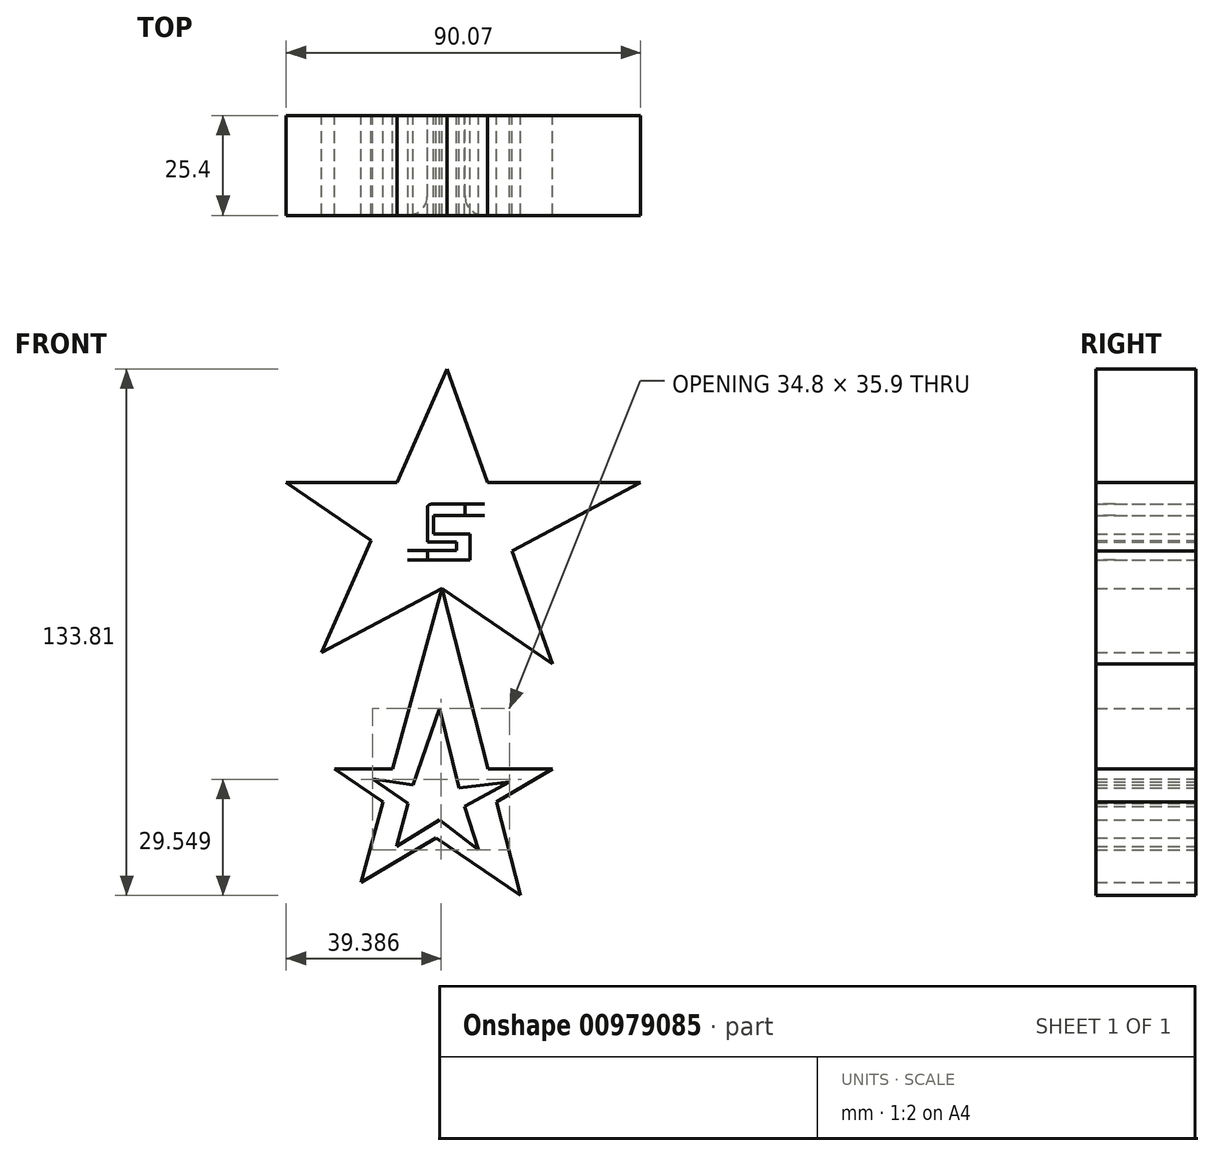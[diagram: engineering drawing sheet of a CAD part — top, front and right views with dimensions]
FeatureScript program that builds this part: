
annotation { "Feature Type Name" : "Feature", "Feature Type Description" : "" }
export const myFeature = defineFeature(function(context is Context, id is Id, definition is map)
    precondition{}
    {
        {
            var Q0;
            Q0=qCreatedBy(makeId("Front.planeOp"),FACE);
            var sketch = newSketch(context, id + "F0", { "sketchPlane" : qUnion([Q0])});
            skLineSegment(sketch, "E0", {"start": v(46.3, 35.13) * mm, "end": v(-40.9, 35.13) * mm});
            skLineSegment(sketch, "E1", {"start": v(-40.9, 35.13) * mm, "end": v(26.84, -10.99) * mm});
            skLineSegment(sketch, "E2", {"start": v(26.84, -10.99) * mm, "end": v(0, 63.95) * mm});
            skLineSegment(sketch, "E3", {"start": v(0, 63.95) * mm, "end": v(-31.89, -8.1) * mm});
            skLineSegment(sketch, "E4", {"start": v(-31.89, -8.1) * mm, "end": v(49.18, 35.13) * mm});
            skLineSegment(sketch, "E5", {"start": v(26.84, -37.65) * mm, "end": v(-28.64, -37.65) * mm});
            skLineSegment(sketch, "E6", {"start": v(-28.64, -37.65) * mm, "end": v(18.67, -69.86) * mm});
            skLineSegment(sketch, "E7", {"start": v(18.67, -69.86) * mm, "end": v(-1.33, 8.2) * mm});
            skLineSegment(sketch, "E8", {"start": v(-1.33, 8.2) * mm, "end": v(-21.8, -66.47) * mm});
            skLineSegment(sketch, "E9", {"start": v(-21.8, -66.47) * mm, "end": v(26.84, -37.65) * mm});
            skLineSegment(sketch, "E10", {"start": v(-40.9, 35.13) * mm, "end": v(49.18, 35.13) * mm});
            skLineSegment(sketch, "E11", {"start": v(-3.4, 28.12) * mm, "end": v(-3.4, 22) * mm});
            skLineSegment(sketch, "E12", {"start": v(-3.4, 22) * mm, "end": v(5.78, 22) * mm});
            skLineSegment(sketch, "E13", {"start": v(5.78, 22) * mm, "end": v(5.78, 15.33) * mm});
            skLineSegment(sketch, "E14", {"start": v(5.78, 15.33) * mm, "end": v(-5.02, 15.33) * mm});
            skLineSegment(sketch, "E15", {"start": v(-5.02, 15.33) * mm, "end": v(-5.02, 17.85) * mm});
            skLineSegment(sketch, "E16", {"start": v(-5.02, 17.85) * mm, "end": v(2.36, 17.85) * mm});
            skLineSegment(sketch, "E17", {"start": v(2.36, 17.85) * mm, "end": v(2.36, 20.01) * mm});
            skLineSegment(sketch, "E18", {"start": v(2.36, 20.01) * mm, "end": v(-5.02, 20.01) * mm});
            skLineSegment(sketch, "E19", {"start": v(-5.02, 20.01) * mm, "end": v(-5.02, 28.57) * mm});
            skLineSegment(sketch, "E20", {"start": v(-4.03, 29.56) * mm, "end": v(4.52, 29.56) * mm});
            skLineSegment(sketch, "E21", {"start": v(-3.4, 26.68) * mm, "end": v(4.52, 26.68) * mm});
            skLineSegment(sketch, "E22", {"start": v(4.52, 29.56) * mm, "end": v(4.52, 26.68) * mm});
            skPoint(sketch, "E23.visualSharp", {"position": v(-5.02, 29.56) * mm});
            skArc(sketch, "E23.filletArc", {"start": v(-4.03, 29.56) * mm, "mid": v(-4.73, 29.27) * mm, "end": v(-5.02, 28.57) * mm});
            skLineSegment(sketch, "E24", {"start": v(-1.98, -22.36) * mm, "end": v(-8.65, -41.75) * mm});
            skLineSegment(sketch, "E25", {"start": v(-1.98, -22.36) * mm, "end": v(3.02, -42.5) * mm});
            skLineSegment(sketch, "E26", {"start": v(-1.98, -50.69) * mm, "end": v(-12.89, -57.35) * mm});
            skLineSegment(sketch, "E27", {"start": v(-12.89, -57.35) * mm, "end": v(-9.88, -46.4) * mm});
            skLineSegment(sketch, "E28", {"start": v(-9.88, -46.4) * mm, "end": v(-18.9, -40.26) * mm});
            skLineSegment(sketch, "E29", {"start": v(-18.9, -40.26) * mm, "end": v(-8.65, -41.75) * mm});
            skLineSegment(sketch, "E30", {"start": v(-1.98, -50.69) * mm, "end": v(8.02, -58.26) * mm});
            skLineSegment(sketch, "E31", {"start": v(8.02, -58.26) * mm, "end": v(4.38, -47.2) * mm});
            skLineSegment(sketch, "E32", {"start": v(3.02, -42.5) * mm, "end": v(15.9, -41) * mm});
            skLineSegment(sketch, "E33", {"start": v(15.9, -41) * mm, "end": v(4.38, -47.2) * mm});
            skSolve(sketch);
        }
        {
            var Q0;
            Q0 = qSketchRegion(id + "F0", true);
            extrude(context, id + "F1", {"entities" : qUnion([Q0]), "depth" : 25.4 * mm, "offsetDistance" : 25.4 * mm});
        }
        {
            var Q0;
            Q0=makeQuery(id+"F1.opExtrude","CAP_EDGE",EDGE,{"disambiguationData":[OSD([sQuery(id+"F0.wireOp",EDGE,"E22")])],"isStart":false});
            var Q1;
            Q1=makeQuery(id+"F1.opExtrude","CAP_EDGE",EDGE,{"disambiguationData":[OSD([sQuery(id+"F0.wireOp",EDGE,"E15")])],"isStart":false});
            fillet(context, id + "F2", {"entities" : qUnion([Q0, Q1]), "radius" : 5 * mm, "tangentPropagation" : true, "allowEdgeOverflow" : false});
        }
    });
